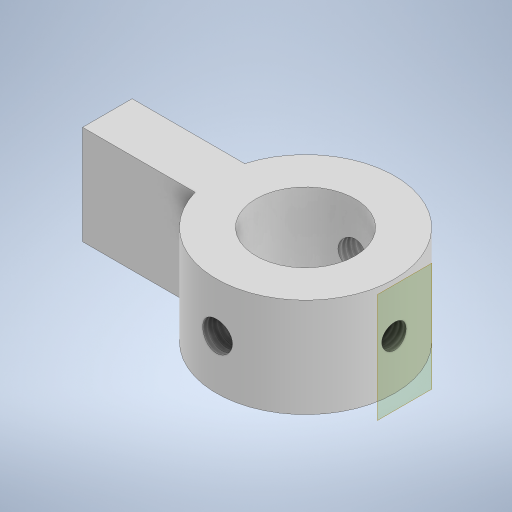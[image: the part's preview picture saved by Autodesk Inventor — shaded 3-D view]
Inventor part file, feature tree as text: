
AUTODESK INVENTOR PART (.ipt)
format: ipt  version: 2023 (Build 270158000, 158)  size: 260,608 bytes
history: native  units: mm
features: sketch x4, other x2, extrude x2, thread x1, hole x1
ambient origin geometry x8: Origin, YZ Plane, XZ Plane, XY Plane, X Axis, Y Axis, Z Axis, Center Point
bodies: Body1 (feature_tree)
feature tree (10):
  other  "Твердое тело1"
  extrude  "Выдавливание1"  Depth=10.0mm
  extrude  "Выдавливание2"  Depth=18.0mm
  thread  "Резьба1"
  other  "РабПлоскость1"
  sketch  "Эскиз3"
  hole  "Отверстие1"  [1 undecoded]
  sketch  "Эскиз1"
  sketch  "Эскиз2"
  sketch  "Эскиз4"
note: 1 required parameter value undecoded (feature->parameter linkage not recoverable at this tier; creation-order binding heuristic only, values carry confidence <= 0.55)
